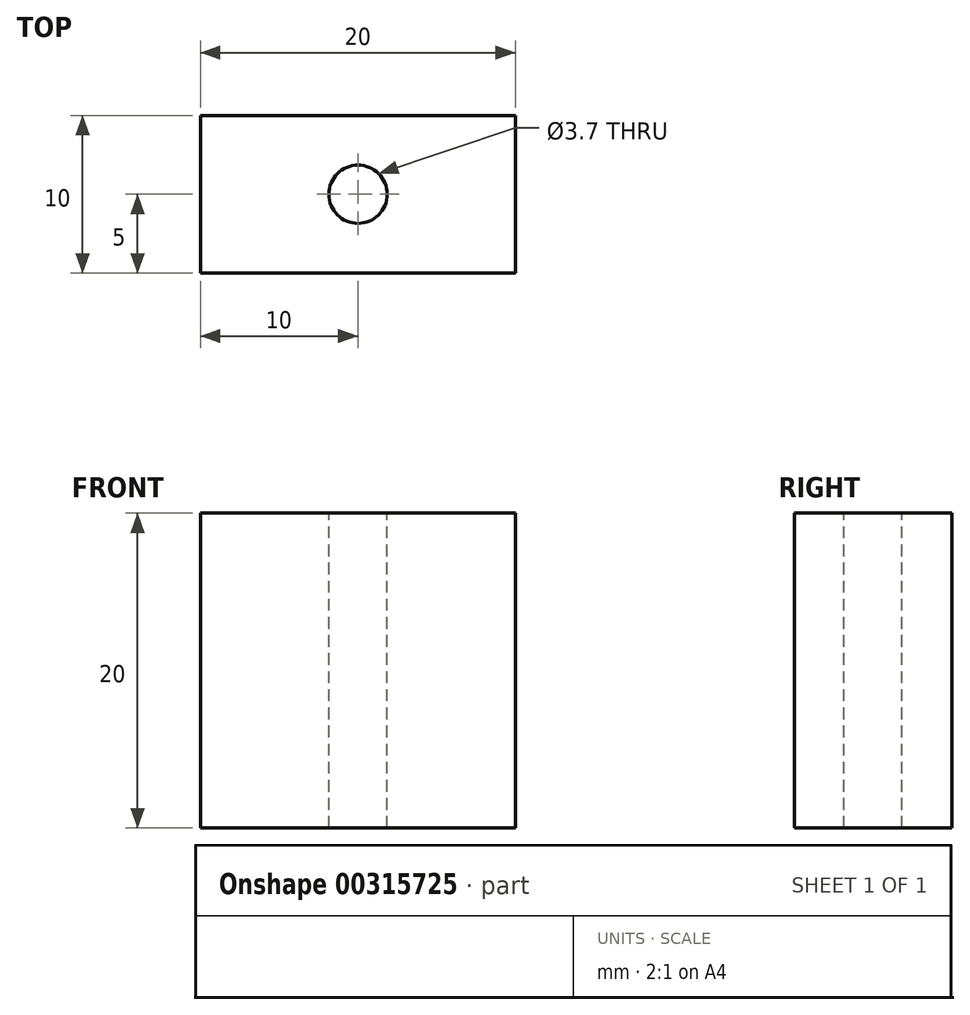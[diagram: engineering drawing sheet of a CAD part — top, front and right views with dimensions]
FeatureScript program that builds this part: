
annotation { "Feature Type Name" : "Feature", "Feature Type Description" : "" }
export const myFeature = defineFeature(function(context is Context, id is Id, definition is map)
    precondition{}
    {
        {
            var Q0;
            Q0=qCreatedBy(makeId("Front.planeOp"),FACE);
            var sketch = newSketch(context, id + "F0", { "sketchPlane" : qUnion([Q0])});
            skLineSegment(sketch, "E0.bottom", {"start": v(-10, 10.25) * mm, "end": v(10, 10.25) * mm});
            skLineSegment(sketch, "E0.top", {"start": v(-10, -9.75) * mm, "end": v(10, -9.75) * mm});
            skLineSegment(sketch, "E0.left", {"start": v(-10, 10.25) * mm, "end": v(-10, -9.75) * mm});
            skLineSegment(sketch, "E0.right", {"start": v(10, 10.25) * mm, "end": v(10, -9.75) * mm});
            skSolve(sketch);
        }
        {
            var Q0;
            Q0 = qSketchRegion(id + "F0", true);
            extrude(context, id + "F1", {"entities" : qUnion([Q0]), "depth" : 10 * mm});
        }
        {
            var Q0;
            Q0=makeQuery(id+"F1.opExtrude","SWEPT_FACE",FACE,{"disambiguationData":[OSD([sQuery(id+"F0.wireOp",EDGE,"E0.bottom")])]});
            var sketch = newSketch(context, id + "F2", { "sketchPlane" : qUnion([Q0])});
            skPoint(sketch, "E1", {"position": v(0, 0) * mm});
            skCircle(sketch, "E2", {"center": v(0, -5) * mm, "radius": 1.85 * mm});
            skSolve(sketch);
        }
        {
            var Q0;
            Q0 = qSketchRegion(id + "F2", true);
            extrude(context, id + "F3", {"entities" : qUnion([Q0]), "operationType" : NewBodyOperationType.REMOVE, "oppositeDirection" : true, "depth" : 25 * mm});
        }
    });
